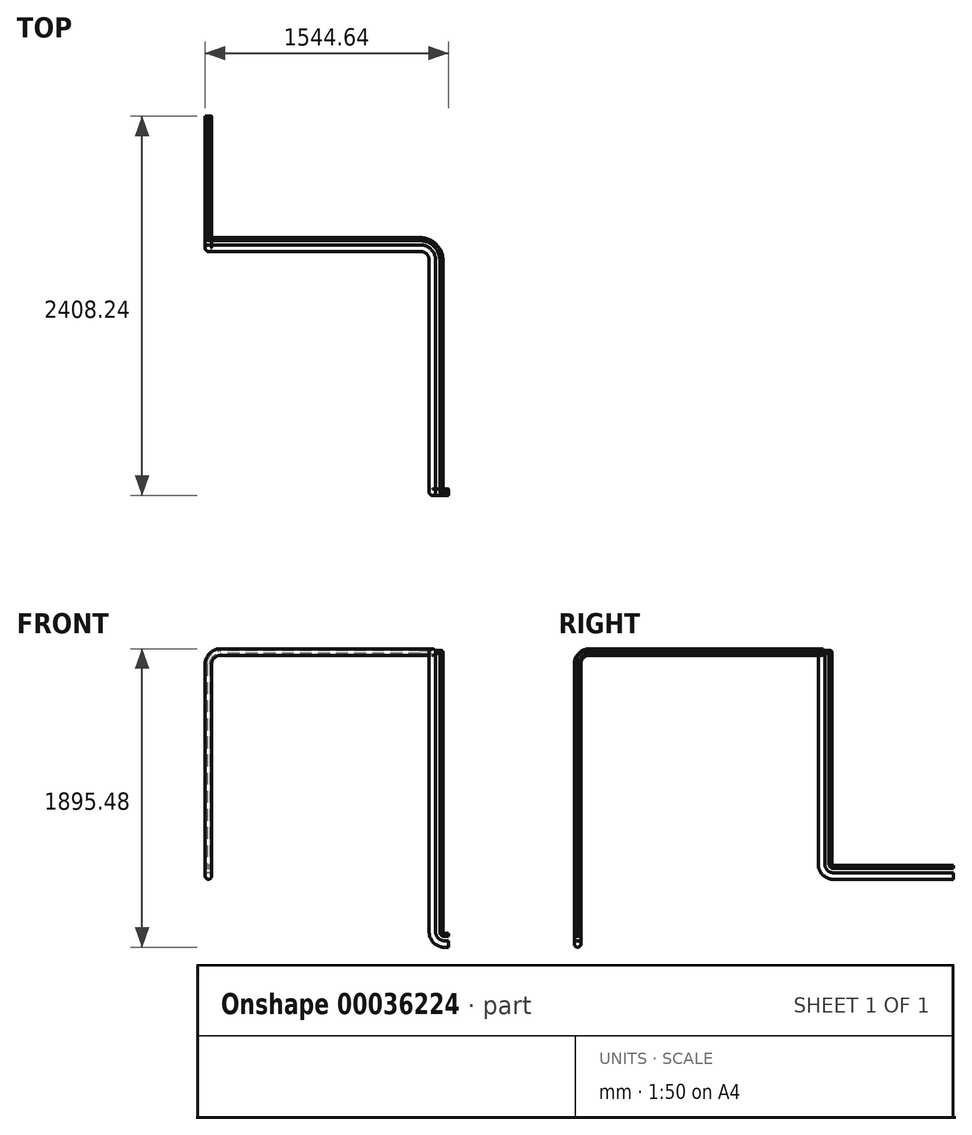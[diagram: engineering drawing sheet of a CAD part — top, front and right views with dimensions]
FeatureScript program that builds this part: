
annotation { "Feature Type Name" : "Feature", "Feature Type Description" : "" }
export const myFeature = defineFeature(function(context is Context, id is Id, definition is map)
    precondition{}
    {
        {
            var Q0;
            Q0=qCreatedBy(makeId("Right.planeOp"),FACE);
            var sketch = newSketch(context, id + "F0", { "sketchPlane" : qUnion([Q0])});
            skCircle(sketch, "E0", {"center": v(0, 0) * mm, "radius": 20.64 * mm});
            skCircle(sketch, "E1", {"center": v(0, 57.15) * mm, "radius": 9.53 * mm});
            skSolve(sketch);
        }
        {
            var Q0;
            Q0=qCreatedBy(makeId("Front.planeOp"),FACE);
            var sketch = newSketch(context, id + "F1", { "sketchPlane" : qUnion([Q0])});
            skLineSegment(sketch, "E2", {"start": v(0, 0) * mm, "end": v(-25.4, 0) * mm});
            skArc(sketch, "E3", {"start": v(-101.6, 76.2) * mm, "mid": v(-79.28, 22.32) * mm, "end": v(-25.4, 0) * mm});
            skLineSegment(sketch, "E4", {"start": v(-101.6, 76.2) * mm, "end": v(-101.6, 1778) * mm});
            skSolve(sketch);
        }
        {
            var Q0;
            Q0=sQuery(id+"F1.wireOp",VERTEX,"E4.end");
            var Q1;
            Q1=qCreatedBy(makeId("Right.planeOp"),FACE);
            cPlane(context, id + "F2", {"entities" : qUnion([Q0, Q1]), "cplaneType" : CPlaneType.PLANE_POINT, "offset" : 152.4 * mm, "width" : 152.4 * mm, "height" : 152.4 * mm});
        }
        {
            var Q0;
            Q0=qCreatedBy(id+"F2.planeOp",FACE);
            var sketch = newSketch(context, id + "F3", { "sketchPlane" : qUnion([Q0])});
            skArc(sketch, "E5", {"start": v(76.2, 1854.2) * mm, "mid": v(22.32, 1831.88) * mm, "end": v(0, 1778) * mm});
            skLineSegment(sketch, "E6", {"start": v(76.2, 1854.2) * mm, "end": v(1473.2, 1854.2) * mm});
            skSolve(sketch);
        }
        {
            var Q0;
            Q0=qCreatedBy(makeId("Top.planeOp"),FACE);
            var Q1;
            Q1=sQuery(id+"F3.wireOp",VERTEX,"E6.end");
            cPlane(context, id + "F4", {"entities" : qUnion([Q0, Q1]), "cplaneType" : CPlaneType.PLANE_POINT, "offset" : 152.4 * mm, "width" : 152.4 * mm, "height" : 152.4 * mm});
        }
        {
            var Q0;
            Q0=qCreatedBy(id+"F4.planeOp",FACE);
            var sketch = newSketch(context, id + "F5", { "sketchPlane" : qUnion([Q0])});
            skArc(sketch, "E7", {"start": v(-101.6, 1473.2) * mm, "mid": v(-123.92, 1527.08) * mm, "end": v(-177.8, 1549.4) * mm});
            skLineSegment(sketch, "E8", {"start": v(-177.8, 1549.4) * mm, "end": v(-1447.8, 1549.4) * mm});
            skSolve(sketch);
        }
        {
            var Q0;
            Q0=qCreatedBy(makeId("Front.planeOp"),FACE);
            var Q1;
            Q1=sQuery(id+"F5.wireOp",VERTEX,"E8.end");
            cPlane(context, id + "F6", {"entities" : qUnion([Q0, Q1]), "cplaneType" : CPlaneType.PLANE_POINT, "offset" : 152.4 * mm, "width" : 152.4 * mm, "height" : 152.4 * mm});
        }
        {
            var Q0;
            Q0=qCreatedBy(id+"F6.planeOp",FACE);
            var sketch = newSketch(context, id + "F7", { "sketchPlane" : qUnion([Q0])});
            skLineSegment(sketch, "E9", {"start": v(-1524, 508) * mm, "end": v(-1524, 1778) * mm});
            skArc(sketch, "E10", {"start": v(-1524, 1778) * mm, "mid": v(-1501.68, 1831.88) * mm, "end": v(-1447.8, 1854.2) * mm});
            skSolve(sketch);
        }
        {
            var Q0;
            Q0=qCreatedBy(makeId("Right.planeOp"),FACE);
            var Q1;
            Q1=sQuery(id+"F7.wireOp",VERTEX,"E9.start");
            cPlane(context, id + "F8", {"entities" : qUnion([Q0, Q1]), "cplaneType" : CPlaneType.PLANE_POINT, "offset" : 152.4 * mm, "width" : 152.4 * mm, "height" : 152.4 * mm});
        }
        {
            var Q0;
            Q0=qCreatedBy(id+"F8.planeOp",FACE);
            var sketch = newSketch(context, id + "F9", { "sketchPlane" : qUnion([Q0])});
            skLineSegment(sketch, "E11", {"start": v(2387.6, 431.8) * mm, "end": v(1625.6, 431.8) * mm});
            skArc(sketch, "E12", {"start": v(1625.6, 431.8) * mm, "mid": v(1571.72, 454.12) * mm, "end": v(1549.4, 508) * mm});
            skSolve(sketch);
        }
        {
            var Q0;
            Q0=qSketchRegion(id+"F0",true);
            var Q1;
            Q1=sQuery(id+"F1.wireOp",EDGE,"E2");
            var Q2;
            Q2=sQuery(id+"F1.wireOp",EDGE,"E3");
            var Q3;
            Q3=sQuery(id+"F1.wireOp",EDGE,"E4");
            var Q4;
            Q4=sQuery(id+"F3.wireOp",EDGE,"E5");
            var Q5;
            Q5=sQuery(id+"F3.wireOp",EDGE,"E6");
            var Q6;
            Q6=sQuery(id+"F5.wireOp",EDGE,"E7");
            var Q7;
            Q7=sQuery(id+"F5.wireOp",EDGE,"E8");
            var Q8;
            Q8=sQuery(id+"F7.wireOp",EDGE,"E10");
            var Q9;
            Q9=sQuery(id+"F7.wireOp",EDGE,"E9");
            var Q10;
            Q10=sQuery(id+"F9.wireOp",EDGE,"E12");
            var Q11;
            Q11=sQuery(id+"F9.wireOp",EDGE,"E11");
            sweep(context, id + "F10", {"profiles" : qUnion([Q0]), "path" : qUnion([Q1, Q2, Q3, Q4, Q5, Q6, Q7, Q8, Q9, Q10, Q11])});
        }
    });
